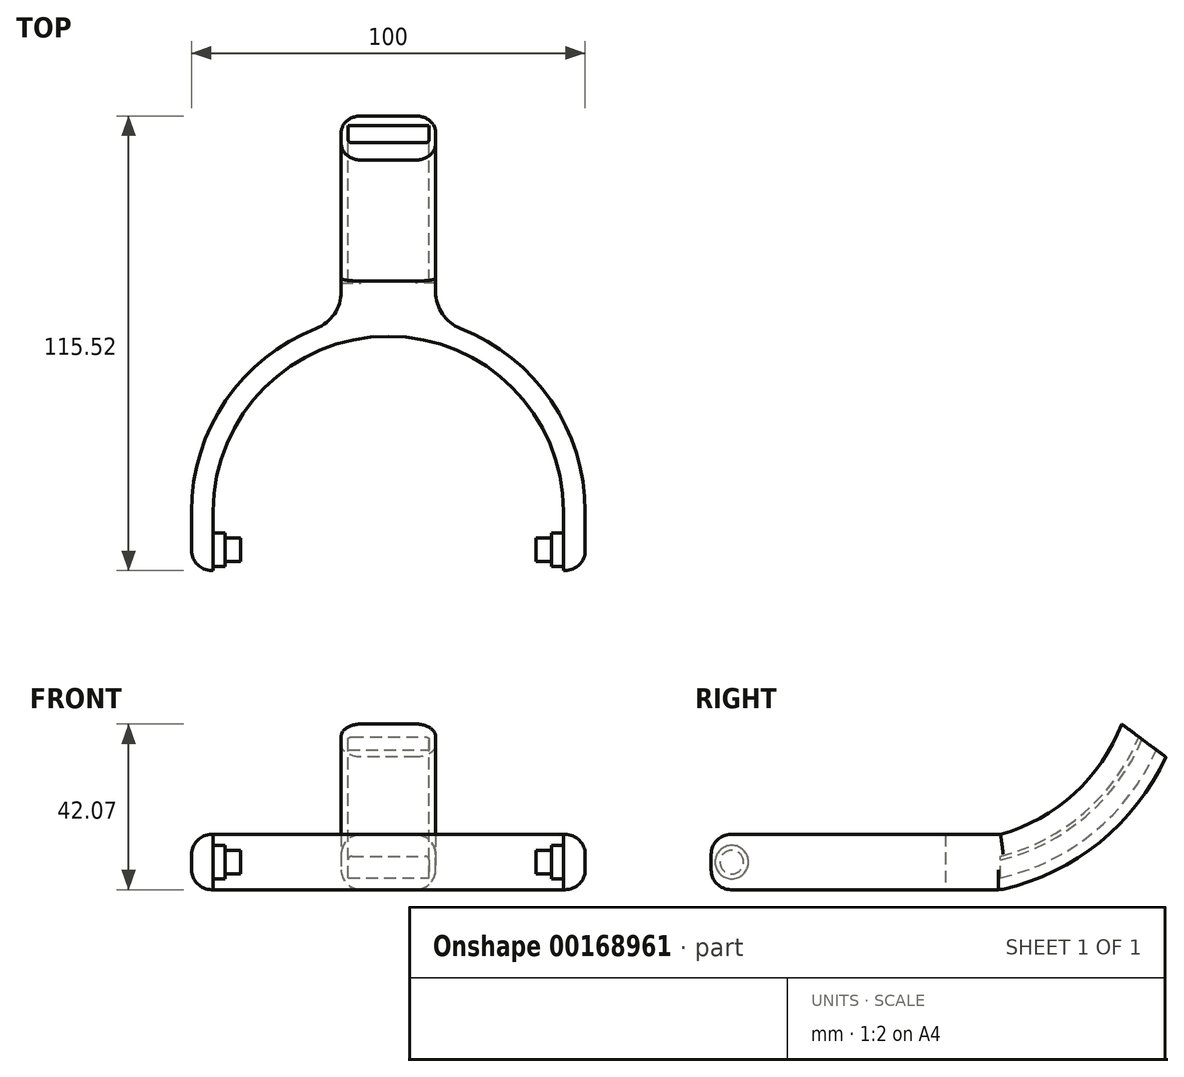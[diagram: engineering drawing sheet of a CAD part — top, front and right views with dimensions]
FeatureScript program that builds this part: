
annotation { "Feature Type Name" : "Feature", "Feature Type Description" : "" }
export const myFeature = defineFeature(function(context is Context, id is Id, definition is map)
    precondition{}
    {
        {
            var Q0;
            Q0=qCreatedBy(makeId("Top.planeOp"),FACE);
            var sketch = newSketch(context, id + "F0", { "sketchPlane" : qUnion([Q0])});
            skArc(sketch, "E0", {"start": v(0, 44.5) * mm, "mid": v(-31.47, 31.47) * mm, "end": v(-44.5, 0) * mm});
            skArc(sketch, "E1", {"start": v(0, 50) * mm, "mid": v(-35.36, 35.36) * mm, "end": v(-50, 0) * mm});
            skLineSegment(sketch, "E2", {"start": v(0, 50) * mm, "end": v(0, 44.5) * mm});
            skLineSegment(sketch, "E3", {"start": v(-50, 0) * mm, "end": v(-44.5, 0) * mm});
            skLineSegment(sketch, "E4", {"start": v(-50, 0) * mm, "end": v(-50, -15) * mm});
            skLineSegment(sketch, "E5", {"start": v(-50, -15) * mm, "end": v(-44.5, -15) * mm});
            skLineSegment(sketch, "E6", {"start": v(-44.5, -15) * mm, "end": v(-44.5, 0) * mm});
            skArc(sketch, "E7.MirrorCS", {"start": v(0, 44.5) * mm, "mid": v(31.47, 31.47) * mm, "end": v(44.5, 0) * mm});
            skArc(sketch, "E8.MirrorCS", {"start": v(0, 50) * mm, "mid": v(35.36, 35.36) * mm, "end": v(50, 0) * mm});
            skLineSegment(sketch, "E9.MirrorCS", {"start": v(50, 0) * mm, "end": v(44.5, 0) * mm});
            skLineSegment(sketch, "E10.MirrorCS", {"start": v(50, 0) * mm, "end": v(50, -15) * mm});
            skLineSegment(sketch, "E11.MirrorCS", {"start": v(44.5, -15) * mm, "end": v(44.5, 0) * mm});
            skLineSegment(sketch, "E12.MirrorCS", {"start": v(50, -15) * mm, "end": v(44.5, -15) * mm});
            skLineSegment(sketch, "E13", {"start": v(-12, 48.54) * mm, "end": v(-12, 58.54) * mm});
            skLineSegment(sketch, "E14", {"start": v(-12, 48.54) * mm, "end": v(12, 48.54) * mm, "construction": true});
            skLineSegment(sketch, "E15", {"start": v(12, 48.54) * mm, "end": v(12, 58.54) * mm});
            skLineSegment(sketch, "E16", {"start": v(12, 58.54) * mm, "end": v(-12, 58.54) * mm});
            skSolve(sketch);
        }
        {
            var Q0;
            Q0 = qSketchRegion(id + "F0", true);
            extrude(context, id + "F1", {"entities" : qUnion([Q0]), "depth" : 14 * mm});
        }
        {
            var Q0;
            Q0=makeQuery(id+"F1.opExtrude","SWEPT_FACE",FACE,{"disambiguationData":[OSD([sQuery(id+"F0.wireOp",EDGE,"E6")])]});
            var sketch = newSketch(context, id + "F2", { "sketchPlane" : qUnion([Q0])});
            skCircle(sketch, "E17", {"center": v(-9.75, 7) * mm, "radius": 4.25 * mm});
            skLineSegment(sketch, "E18", {"start": v(-15, 0) * mm, "end": v(0, 0) * mm});
            skCircle(sketch, "E19", {"center": v(-9.75, 7) * mm, "radius": 3 * mm});
            skSolve(sketch);
        }
        {
            var Q0;
            Q0=makeQuery(id+"F2.imprint","IMPRINT",FACE,{"disambiguationData":[TD([[makeQuery(id+"F2.imprint","IMPRINT",EDGE,{"derivedFrom":sQuery(id+"F2.wireOp",EDGE,"E17")}),1.0]])]});
            extrude(context, id + "F3", {"entities" : qUnion([Q0]), "operationType" : NewBodyOperationType.ADD, "depth" : 3 * mm});
        }
        {
            var Q0;
            Q0=makeQuery(id+"F3.boolean.opBoolean","SPLIT",FACE,{"disambiguationData":[TD([makeQuery(id+"F3.opExtrude","SWEPT_FACE",FACE,{"disambiguationData":[OSD([sQuery(id+"F2.wireOp",EDGE,"E19")])]})])],"derivedFrom":makeQuery(id+"F1.opExtrude","SWEPT_FACE",FACE,{"disambiguationData":[OSD([sQuery(id+"F0.wireOp",EDGE,"E6")])]})});
            extrude(context, id + "F4", {"entities" : qUnion([Q0]), "operationType" : NewBodyOperationType.ADD, "depth" : 7 * mm});
        }
        {
            var Q0;
            Q0=makeQuery(id+"F1.opExtrude","SWEPT_BODY",BODY,{"disambiguationData":[OSD([sQuery(id+"F0.wireOp",EDGE,"E0"),sQuery(id+"F0.wireOp",EDGE,"E1"),sQuery(id+"F0.wireOp",EDGE,"E4"),sQuery(id+"F0.wireOp",EDGE,"E5"),sQuery(id+"F0.wireOp",EDGE,"E6"),sQuery(id+"F0.wireOp",EDGE,"E7.MirrorCS"),sQuery(id+"F0.wireOp",EDGE,"E8.MirrorCS"),sQuery(id+"F0.wireOp",EDGE,"E10.MirrorCS"),sQuery(id+"F0.wireOp",EDGE,"E11.MirrorCS"),sQuery(id+"F0.wireOp",EDGE,"E12.MirrorCS")])]});
            var Q1;
            Q1=qCreatedBy(makeId("Right.planeOp"),FACE);
            mirror(context, id + "F5", {"operationType" : NewBodyOperationType.ADD, "entities" : qUnion([Q0]), "mirrorPlane" : qUnion([Q1])});
        }
        {
            var Q0;
            Q0=makeQuery(id+"F1.opExtrude","SWEPT_FACE",FACE,{"disambiguationData":[OSD([sQuery(id+"F0.wireOp",EDGE,"E16")])]});
            var sketch = newSketch(context, id + "F6", { "sketchPlane" : qUnion([Q0])});
            skLineSegment(sketch, "E20", {"start": v(10.25, 3) * mm, "end": v(-10.35, 3) * mm});
            skLineSegment(sketch, "E21", {"start": v(10.25, 3) * mm, "end": v(10.25, 7.5) * mm});
            skLineSegment(sketch, "E22", {"start": v(9.25, 8.5) * mm, "end": v(-9.35, 8.5) * mm});
            skLineSegment(sketch, "E23", {"start": v(-10.35, 7.5) * mm, "end": v(-10.35, 3) * mm});
            skLineSegment(sketch, "E24", {"start": v(0, 0) * mm, "end": v(0, 3) * mm, "construction": true});
            skLineSegment(sketch, "E25", {"start": v(10.25, 3.86) * mm, "end": v(12, 3.86) * mm, "construction": true});
            skPoint(sketch, "E26.visualSharp", {"position": v(10.25, 8.5) * mm});
            skArc(sketch, "E26.filletArc", {"start": v(10.25, 7.5) * mm, "mid": v(9.96, 8.2) * mm, "end": v(9.25, 8.5) * mm});
            skPoint(sketch, "E27.visualSharp", {"position": v(-10.35, 8.5) * mm});
            skArc(sketch, "E27.filletArc", {"start": v(-9.35, 8.5) * mm, "mid": v(-10.06, 8.2) * mm, "end": v(-10.35, 7.5) * mm});
            skSolve(sketch);
        }
        {
            var Q0;
            Q0=makeQuery(id+"F1.opExtrude","SWEPT_FACE",FACE,{"disambiguationData":[OSD([sQuery(id+"F0.wireOp",EDGE,"E15")])]});
            var sketch = newSketch(context, id + "F7", { "sketchPlane" : qUnion([Q0])});
            skArc(sketch, "E28", {"start": v(58.54, 0) * mm, "mid": v(83.52, 11.88) * mm, "end": v(100.52, 33.7) * mm});
            skSolve(sketch);
        }
        {
            var Q0;
            Q0=makeQuery(id+"F6.imprint","IMPRINT",FACE,{"disambiguationData":[TD([[makeQuery(id+"F6.imprint","IMPRINT",EDGE,{"derivedFrom":sQuery(id+"F6.wireOp",EDGE,"E20")}),1.0]])]});
            var Q1;
            Q1=sQuery(id+"F7.wireOp",EDGE,"E28");
            sweep(context, id + "F8", {"operationType" : NewBodyOperationType.ADD, "profiles" : qUnion([Q0]), "path" : qUnion([Q1])});
        }
        {
            var Q0;
            Q0=makeQuery(id+"F1.opExtrude","SWEPT_EDGE",EDGE,{"disambiguationData":[OSD([sQuery(id+"F0.wireOp",EDGE,"E10.MirrorCS"),sQuery(id+"F0.wireOp",EDGE,"E12.MirrorCS")])]});
            fillet(context, id + "F9", {"entities" : qUnion([Q0]), "radius" : 5.08 * mm, "tangentPropagation" : true, "allowEdgeOverflow" : false});
        }
        {
            var Q0;
            Q0=makeQuery(id+"F1.opExtrude","SWEPT_EDGE",EDGE,{"disambiguationData":[OSD([sQuery(id+"F0.wireOp",EDGE,"E4"),sQuery(id+"F0.wireOp",EDGE,"E5")])]});
            fillet(context, id + "F10", {"entities" : qUnion([Q0]), "radius" : 5.08 * mm, "tangentPropagation" : true, "allowEdgeOverflow" : false});
        }
        {
            var Q0;
            Q0=makeQuery(id+"F1.opExtrude","SWEPT_EDGE",EDGE,{"disambiguationData":[OSD([sQuery(id+"F0.wireOp",EDGE,"E8.MirrorCS"),sQuery(id+"F0.wireOp",EDGE,"E15")])]});
            var Q1;
            Q1=makeQuery(id+"F1.opExtrude","SWEPT_EDGE",EDGE,{"disambiguationData":[OSD([sQuery(id+"F0.wireOp",EDGE,"E1"),sQuery(id+"F0.wireOp",EDGE,"E13")])]});
            fillet(context, id + "F11", {"entities" : qUnion([Q0, Q1]), "radius" : 10 * mm, "tangentPropagation" : true, "allowEdgeOverflow" : false});
        }
        {
            var Q0;
            Q0=makeQuery(id+"F1.opExtrude","CAP_EDGE",EDGE,{"disambiguationData":[OSD([sQuery(id+"F0.wireOp",EDGE,"E1")])],"isStart":true});
            var Q1;
            Q1=makeQuery(id+"F1.opExtrude","CAP_EDGE",EDGE,{"disambiguationData":[OSD([sQuery(id+"F0.wireOp",EDGE,"E8.MirrorCS")])],"isStart":true});
            fillet(context, id + "F12", {"entities" : qUnion([Q0, Q1]), "radius" : 5.08 * mm, "tangentPropagation" : true, "allowEdgeOverflow" : false});
        }
        {
            var Q0;
            {var subQ0=sQuery(id+"F7.wireOp",EDGE,"E28");var subQ1=sQuery(id+"F0.wireOp",EDGE,"E16");var subQ2=sQuery(id+"F0.wireOp",EDGE,"E13");Q0=makeQuery(id+"F8.opSweep","SWEPT_EDGE",EDGE,{"disambiguationData":[OSD([subQ2,subQ1,subQ0]),TDD([makeQuery(id+"F6.imprint","INTERSECT",VERTEX,{"derivedFrom":[makeQuery(id+"F1.opExtrude","SWEPT_EDGE",EDGE,{"disambiguationData":[OSD([subQ2,subQ1])]}),makeQuery(id+"F1.opExtrude","CAP_EDGE",EDGE,{"disambiguationData":[OSD([subQ1])],"isStart":true})]}),subQ0])]});}
            var Q1;
            {var subQ0=sQuery(id+"F7.wireOp",EDGE,"E28");var subQ1=sQuery(id+"F0.wireOp",EDGE,"E16");var subQ2=sQuery(id+"F0.wireOp",EDGE,"E15");Q1=makeQuery(id+"F8.opSweep","SWEPT_EDGE",EDGE,{"disambiguationData":[OSD([subQ2,subQ1,subQ0]),TDD([makeQuery(id+"F6.imprint","INTERSECT",VERTEX,{"derivedFrom":[makeQuery(id+"F1.opExtrude","SWEPT_EDGE",EDGE,{"disambiguationData":[OSD([subQ2,subQ1])]}),makeQuery(id+"F1.opExtrude","CAP_EDGE",EDGE,{"disambiguationData":[OSD([subQ1])],"isStart":false})]}),subQ0])]});}
            var Q2;
            {var subQ0=sQuery(id+"F7.wireOp",EDGE,"E28");var subQ1=sQuery(id+"F0.wireOp",EDGE,"E16");var subQ2=sQuery(id+"F0.wireOp",EDGE,"E13");Q2=makeQuery(id+"F8.opSweep","SWEPT_EDGE",EDGE,{"disambiguationData":[OSD([subQ2,subQ1,subQ0]),TDD([makeQuery(id+"F6.imprint","INTERSECT",VERTEX,{"derivedFrom":[makeQuery(id+"F1.opExtrude","SWEPT_EDGE",EDGE,{"disambiguationData":[OSD([subQ2,subQ1])]}),makeQuery(id+"F1.opExtrude","CAP_EDGE",EDGE,{"disambiguationData":[OSD([subQ1])],"isStart":false})]}),subQ0])]});}
            var Q3;
            {var subQ0=sQuery(id+"F0.wireOp",EDGE,"E15");var subQ1=sQuery(id+"F0.wireOp",EDGE,"E8.MirrorCS");Q3=makeQuery(id+"F11.opFillet","BLEND_EDGE",EDGE,{"blendedFrom":[makeQuery(id+"F1.opExtrude","SWEPT_EDGE",EDGE,{"disambiguationData":[OSD([subQ1,subQ0])]}),makeQuery(id+"F1.opExtrude","CAP_FACE",FACE,{"disambiguationData":[OSD([sQuery(id+"F0.wireOp",EDGE,"E0"),sQuery(id+"F0.wireOp",EDGE,"E1"),sQuery(id+"F0.wireOp",EDGE,"E4"),sQuery(id+"F0.wireOp",EDGE,"E5"),sQuery(id+"F0.wireOp",EDGE,"E6"),sQuery(id+"F0.wireOp",EDGE,"E7.MirrorCS"),subQ1,sQuery(id+"F0.wireOp",EDGE,"E10.MirrorCS"),sQuery(id+"F0.wireOp",EDGE,"E11.MirrorCS"),sQuery(id+"F0.wireOp",EDGE,"E12.MirrorCS"),sQuery(id+"F0.wireOp",EDGE,"E13"),subQ0,sQuery(id+"F0.wireOp",EDGE,"E16")])],"isStart":false})],"blendedInto":[makeQuery(id+"F1.opExtrude","CAP_FACE",FACE,{"disambiguationData":[OSD([sQuery(id+"F0.wireOp",EDGE,"E0"),sQuery(id+"F0.wireOp",EDGE,"E1"),sQuery(id+"F0.wireOp",EDGE,"E4"),sQuery(id+"F0.wireOp",EDGE,"E5"),sQuery(id+"F0.wireOp",EDGE,"E6"),sQuery(id+"F0.wireOp",EDGE,"E7.MirrorCS"),subQ1,sQuery(id+"F0.wireOp",EDGE,"E10.MirrorCS"),sQuery(id+"F0.wireOp",EDGE,"E11.MirrorCS"),sQuery(id+"F0.wireOp",EDGE,"E12.MirrorCS"),sQuery(id+"F0.wireOp",EDGE,"E13"),subQ0,sQuery(id+"F0.wireOp",EDGE,"E16")])],"isStart":false})]});}
            var Q4;
            {var subQ0=sQuery(id+"F0.wireOp",EDGE,"E13");var subQ1=sQuery(id+"F0.wireOp",EDGE,"E1");Q4=makeQuery(id+"F11.opFillet","BLEND_EDGE",EDGE,{"blendedFrom":[makeQuery(id+"F1.opExtrude","SWEPT_EDGE",EDGE,{"disambiguationData":[OSD([subQ1,subQ0])]}),makeQuery(id+"F1.opExtrude","CAP_FACE",FACE,{"disambiguationData":[OSD([sQuery(id+"F0.wireOp",EDGE,"E0"),subQ1,sQuery(id+"F0.wireOp",EDGE,"E4"),sQuery(id+"F0.wireOp",EDGE,"E5"),sQuery(id+"F0.wireOp",EDGE,"E6"),sQuery(id+"F0.wireOp",EDGE,"E7.MirrorCS"),sQuery(id+"F0.wireOp",EDGE,"E8.MirrorCS"),sQuery(id+"F0.wireOp",EDGE,"E10.MirrorCS"),sQuery(id+"F0.wireOp",EDGE,"E11.MirrorCS"),sQuery(id+"F0.wireOp",EDGE,"E12.MirrorCS"),subQ0,sQuery(id+"F0.wireOp",EDGE,"E15"),sQuery(id+"F0.wireOp",EDGE,"E16")])],"isStart":false})],"blendedInto":[makeQuery(id+"F1.opExtrude","CAP_FACE",FACE,{"disambiguationData":[OSD([sQuery(id+"F0.wireOp",EDGE,"E0"),subQ1,sQuery(id+"F0.wireOp",EDGE,"E4"),sQuery(id+"F0.wireOp",EDGE,"E5"),sQuery(id+"F0.wireOp",EDGE,"E6"),sQuery(id+"F0.wireOp",EDGE,"E7.MirrorCS"),sQuery(id+"F0.wireOp",EDGE,"E8.MirrorCS"),sQuery(id+"F0.wireOp",EDGE,"E10.MirrorCS"),sQuery(id+"F0.wireOp",EDGE,"E11.MirrorCS"),sQuery(id+"F0.wireOp",EDGE,"E12.MirrorCS"),subQ0,sQuery(id+"F0.wireOp",EDGE,"E15"),sQuery(id+"F0.wireOp",EDGE,"E16")])],"isStart":false})]});}
            fillet(context, id + "F13", {"entities" : qUnion([Q0, Q1, Q2, Q3, Q4]), "radius" : 5.08 * mm, "tangentPropagation" : true, "allowEdgeOverflow" : false});
        }
    });
